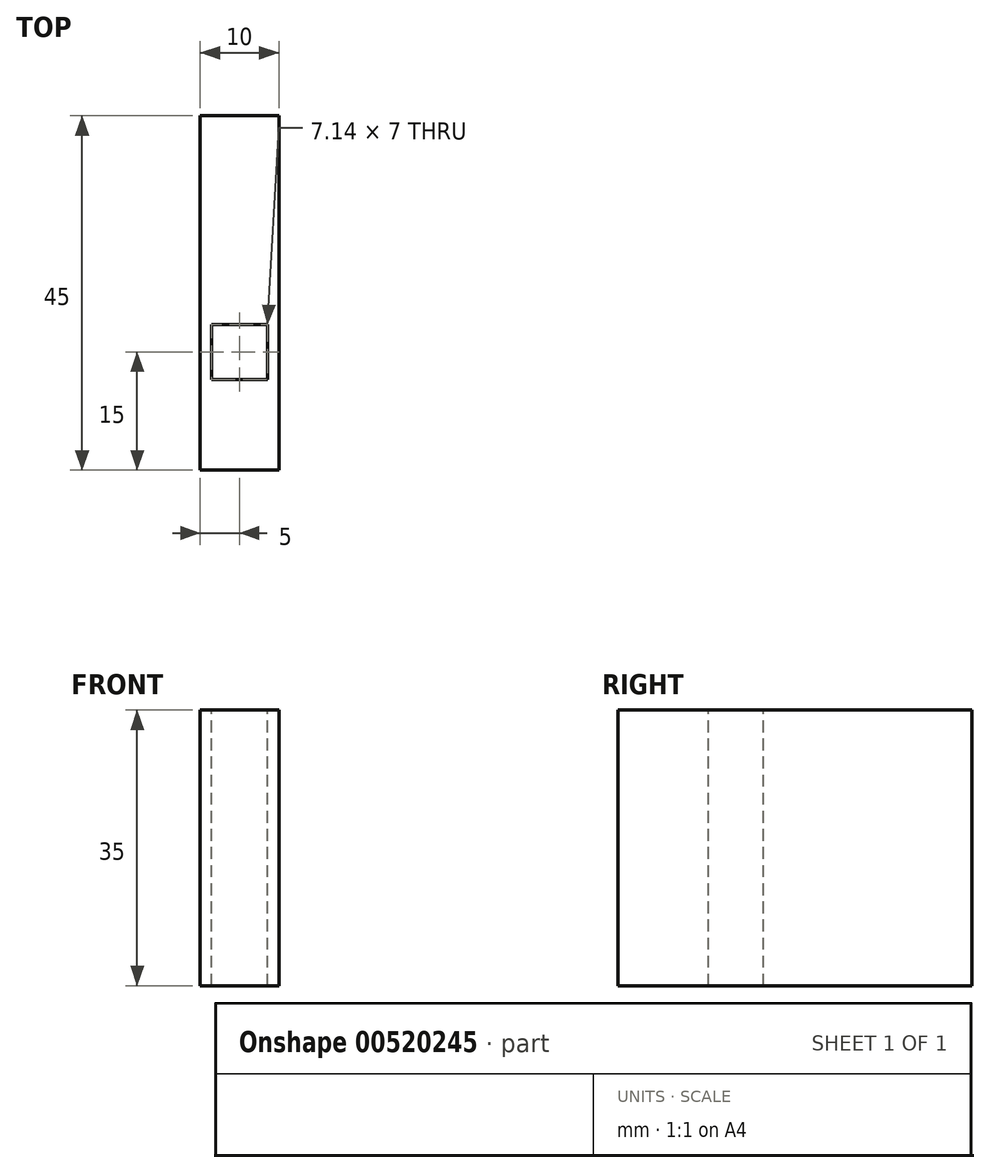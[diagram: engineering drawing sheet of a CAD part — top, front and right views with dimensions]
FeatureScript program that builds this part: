
annotation { "Feature Type Name" : "Feature", "Feature Type Description" : "" }
export const myFeature = defineFeature(function(context is Context, id is Id, definition is map)
    precondition{}
    {
        {
            var Q0;
            Q0=qCreatedBy(makeId("Top.planeOp"),FACE);
            var sketch = newSketch(context, id + "F0", { "sketchPlane" : qUnion([Q0])});
            skLineSegment(sketch, "E0.bottom", {"start": v(0, 0) * mm, "end": v(10, 0) * mm});
            skLineSegment(sketch, "E0.top", {"start": v(0, 20) * mm, "end": v(10, 20) * mm});
            skLineSegment(sketch, "E0.left", {"start": v(0, 0) * mm, "end": v(0, 20) * mm});
            skLineSegment(sketch, "E0.right", {"start": v(10, 0) * mm, "end": v(10, 20) * mm});
            skSolve(sketch);
        }
        {
            var Q0;
            Q0=makeQuery(id+"F0.imprint","IMPRINT",FACE,{"disambiguationData":[TD([[makeQuery(id+"F0.imprint","IMPRINT",EDGE,{"derivedFrom":sQuery(id+"F0.wireOp",EDGE,"E0.bottom")}),1.0]])]});
            var Q1;
            Q1 = qSketchRegion(id + "F0", true);
            extrude(context, id + "F1", {"entities" : qUnion([Q0, Q1]), "depth" : 10 * mm, "offsetDistance" : 25 * mm});
        }
        {
            var Q0;
            Q0=makeQuery(id+"F1.opExtrude","CAP_FACE",FACE,{"disambiguationData":[OSD([sQuery(id+"F0.wireOp",EDGE,"E0.bottom"),sQuery(id+"F0.wireOp",EDGE,"E0.top"),sQuery(id+"F0.wireOp",EDGE,"E0.left"),sQuery(id+"F0.wireOp",EDGE,"E0.right")])],"isStart":false});
            var sketch = newSketch(context, id + "F2", { "sketchPlane" : qUnion([Q0])});
            skLineSegment(sketch, "E1.bottom", {"start": v(1.43, 11.5) * mm, "end": v(8.57, 11.5) * mm});
            skLineSegment(sketch, "E1.top", {"start": v(1.43, 18.5) * mm, "end": v(8.57, 18.5) * mm});
            skLineSegment(sketch, "E1.left", {"start": v(1.43, 11.5) * mm, "end": v(1.43, 18.5) * mm});
            skLineSegment(sketch, "E1.right", {"start": v(8.57, 11.5) * mm, "end": v(8.57, 18.5) * mm});
            skSolve(sketch);
        }
        {
            var Q0;
            Q0 = qSketchRegion(id + "F2", true);
            extrude(context, id + "F3", {"entities" : qUnion([Q0]), "operationType" : NewBodyOperationType.REMOVE, "oppositeDirection" : true, "depth" : 25 * mm, "offsetDistance" : 25 * mm});
        }
        {
            var Q0;
            Q0=makeQuery(id+"F1.opExtrude","SWEPT_FACE",FACE,{"disambiguationData":[OSD([sQuery(id+"F0.wireOp",EDGE,"E0.top")])]});
            extrude(context, id + "F4", {"entities" : qUnion([Q0]), "operationType" : NewBodyOperationType.ADD, "depth" : 25 * mm, "offsetDistance" : 25 * mm});
        }
        {
            var Q0;
            {var subQ0=sQuery(id+"F0.wireOp",EDGE,"E0.top");Q0=makeQuery(id+"F4.boolean.opBoolean","MERGE",FACE,{"derivedFrom":[makeQuery(id+"F1.opExtrude","CAP_FACE",FACE,{"disambiguationData":[OSD([sQuery(id+"F0.wireOp",EDGE,"E0.bottom"),subQ0,sQuery(id+"F0.wireOp",EDGE,"E0.left"),sQuery(id+"F0.wireOp",EDGE,"E0.right")])],"isStart":false}),makeQuery(id+"F4.opExtrude","SWEPT_FACE",FACE,{"disambiguationData":[OSD([subQ0]),TDD([makeQuery(id+"F1.opExtrude","CAP_EDGE",EDGE,{"disambiguationData":[OSD([subQ0])],"isStart":false})])]})]});}
            extrude(context, id + "F5", {"entities" : qUnion([Q0]), "operationType" : NewBodyOperationType.ADD, "depth" : 25 * mm, "offsetDistance" : 25 * mm});
        }
    });
